# Revit family: Graypants_Scraplights_Classics_Nest_24_32_Pendant_R21_0925
name_source: partatom
category: Lighting Fixtures
units: mm (PartAtom-declared; Revit-internal decimal feet)

## family parameters
Cut with Voids When Loaded = No
Host = Face
Light Source = Yes
Part Type = Normal
Room Calculation Point = No
Round Connector Dimension = Use Diameter
Shared = No

## types (2) — shared parameters
Color Filter = 16777215
Default Elevation = 4' - 0"
Dimming Lamp Color Temperature Shift = <None>
Graypants_Cord/Canopy_Finish_Options = White | Black
Graypants_Manufacturer = Graypants
Graypants_Shade_Finish_Options = Natural Cardboard | Blonde Cardboard | White Cardboard
Graypants_URL = www.graypants.com

## per-type parameters (varying)
| type | Emit from Line Length | Graypants_Model | Graypants_Nest24_Canopy_Visible | Graypants_Nest24_Cord_Visible | Graypants_Nest24_Shade_Visible | Graypants_Nest32_Canopy_Visible | Graypants_Nest32_Cord_Visible | Graypants_Nest32_Shade_Visible | Light Source Symbol Size |
| Graypants_Scraplights_Nest24_Pendant | 2' - 1 9/32" | Scraplights_Classics_Nest_24 | Yes | Yes | Yes | No | No | No | 0' - 9" |
| Graypants_Scraplights_Nest32_Pendant | 2' - 9 21/32" | Scraplights_Classics_Nest_32 | No | No | No | Yes | Yes | Yes | 1' - 1" |

## geometry (parser evidence)
native form markers: Sweep x12
no freeform markers — native parametric forms only
